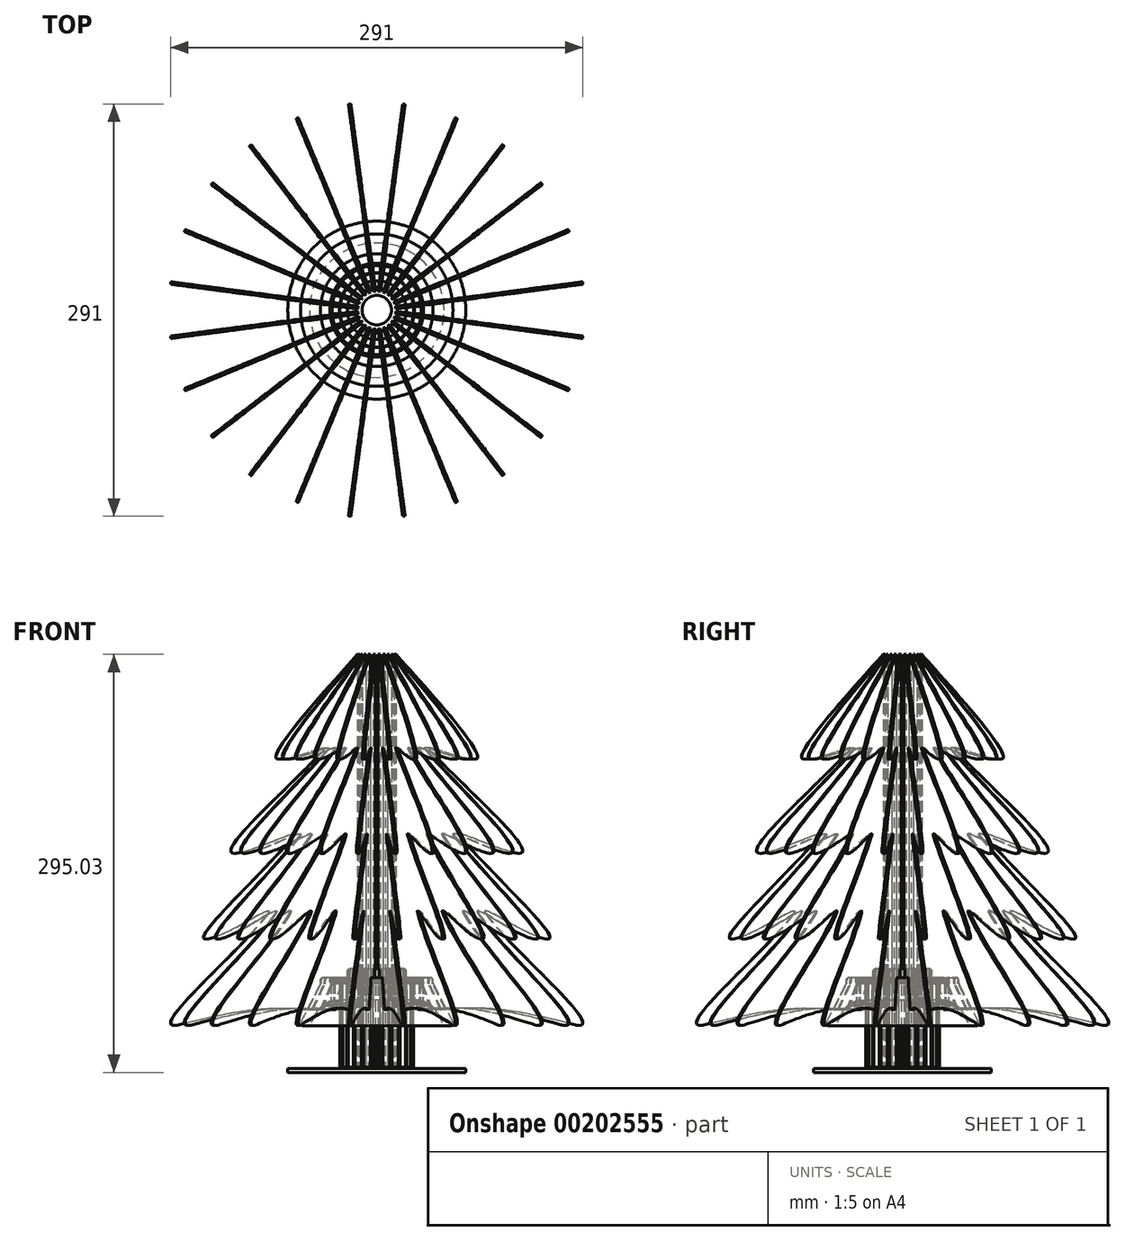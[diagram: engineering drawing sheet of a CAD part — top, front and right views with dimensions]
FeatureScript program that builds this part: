
annotation { "Feature Type Name" : "Feature", "Feature Type Description" : "" }
export const myFeature = defineFeature(function(context is Context, id is Id, definition is map)
    precondition{}
    {
        {
            var Q0;
            Q0=qCreatedBy(makeId("Top.planeOp"),FACE);
            var sketch = newSketch(context, id + "F0", { "sketchPlane" : qUnion([Q0])});
            skCircle(sketch, "E0", {"center": v(0, 0) * mm, "radius": 32.75 * mm});
            skCircle(sketch, "E1", {"center": v(0, 0) * mm, "radius": 26.1 * mm});
            skSolve(sketch);
        }
        {
            var Q0;
            Q0=qSketchRegion(id+"F0",true);
            extrude(context, id + "F1", {"entities" : qUnion([Q0]), "depth" : 1.65 * mm});
        }
        {
            var Q0;
            Q0=makeQuery(id+"F1.opExtrude","CAP_FACE",FACE,{"disambiguationData":[OSD([sQuery(id+"F0.wireOp",EDGE,"E0"),sQuery(id+"F0.wireOp",EDGE,"E1")])],"isStart":false});
            var sketch = newSketch(context, id + "F2", { "sketchPlane" : qUnion([Q0])});
            skLineSegment(sketch, "E2.bottom", {"start": v(2.5, -26.5) * mm, "end": v(-2.5, -26.5) * mm});
            skLineSegment(sketch, "E2.top", {"start": v(2.5, -31.5) * mm, "end": v(-2.5, -31.5) * mm});
            skLineSegment(sketch, "E2.left", {"start": v(2.5, -26.5) * mm, "end": v(2.5, -31.5) * mm});
            skLineSegment(sketch, "E2.right", {"start": v(-2.5, -26.5) * mm, "end": v(-2.5, -31.5) * mm});
            skPoint(sketch, "E2.middle", {"position": v(0, -29) * mm});
            skSolve(sketch);
        }
        {
            var Q0;
            Q0=makeQuery(id+"F2.imprint","IMPRINT",FACE,{"disambiguationData":[TD([[makeQuery(id+"F2.imprint","IMPRINT",EDGE,{"derivedFrom":sQuery(id+"F2.wireOp",EDGE,"E2.bottom")}),1.0]])]});
            extrude(context, id + "F3", {"entities" : qUnion([Q0]), "depth" : 1.62 * mm});
        }
        {
            var Q0;
            Q0=makeQuery(id+"F3.opExtrude","SWEPT_BODY",BODY,{"disambiguationData":[OSD([sQuery(id+"F2.wireOp",EDGE,"E2.bottom"),sQuery(id+"F2.wireOp",EDGE,"E2.top"),sQuery(id+"F2.wireOp",EDGE,"E2.left"),sQuery(id+"F2.wireOp",EDGE,"E2.right")])]});
            var Q1;
            Q1=makeQuery(id+"F1.opExtrude","CAP_EDGE",EDGE,{"disambiguationData":[OSD([sQuery(id+"F0.wireOp",EDGE,"E0")])],"isStart":false});
            circularPattern(context, id + "F4", {"entities" : qUnion([Q0]), "axis" : qUnion([Q1]), "angle" : 360 * degree, "instanceCount" : 24, "equalSpace" : true});
        }
        {
            var Q0;
            Q0=qCreatedBy(makeId("Front.planeOp"),FACE);
            var sketch = newSketch(context, id + "F5", { "sketchPlane" : qUnion([Q0])});
            skFitSpline(sketch, "E3", {"points": [v(-35, 220) * mm, v(-100, 30) * mm, v(-35, 0) * mm, v(-35, -60) * mm], "startDerivative": vector(15.54, -139.11) * mm, "endDerivative": vector(560.9, -352.96) * mm});
            skLineSegment(sketch, "E4", {"start": v(-9.97, -59.99) * mm, "end": v(-9.97, -0.01) * mm, "construction": true});
            skLineSegment(sketch, "E5", {"start": v(-9.97, -0.01) * mm, "end": v(-33, -0.01) * mm});
            skLineSegment(sketch, "E6", {"start": v(-33, -0.01) * mm, "end": v(-33, 3.46) * mm});
            skLineSegment(sketch, "E7", {"start": v(-33, 3.46) * mm, "end": v(0, 3.46) * mm});
            skLineSegment(sketch, "E8", {"start": v(0, 3.46) * mm, "end": v(0, 369.62) * mm, "construction": true});
            skLineSegment(sketch, "E9", {"start": v(-5, 3.46) * mm, "end": v(-5, 220) * mm, "construction": true});
            skFitSpline(sketch, "E10", {"points": [v(-5, -60) * mm, v(-5, 0) * mm, v(-70, 30) * mm, v(-5, 220) * mm], "startDerivative": vector(-560.9, 352.96) * mm, "endDerivative": vector(-15.54, 139.11) * mm});
            skLineSegment(sketch, "E11", {"start": v(-35, -60) * mm, "end": v(-5, -60) * mm});
            skLineSegment(sketch, "E12", {"start": v(-82.67, -30) * mm, "end": v(-52.67, -30) * mm, "construction": true});
            skLineSegment(sketch, "E13", {"start": v(-35, 0) * mm, "end": v(-5, 0) * mm, "construction": true});
            skLineSegment(sketch, "E14", {"start": v(-35, 220) * mm, "end": v(-5, 220) * mm});
            skLineSegment(sketch, "E15", {"start": v(-32.58, 198.37) * mm, "end": v(-2.58, 198.37) * mm, "construction": true});
            skLineSegment(sketch, "E16", {"start": v(-100, 30) * mm, "end": v(-70, 30) * mm, "construction": true});
            skPoint(sketch, "E17", {"position": v(-9.97, -30) * mm});
            skSolve(sketch);
        }
        {
            var Q0;
            Q0=qCreatedBy(makeId("Front.planeOp"),FACE);
            var sketch = newSketch(context, id + "F6", { "sketchPlane" : qUnion([Q0])});
            skFitSpline(sketch, "E18", {"points": [v(13.6, 232.09) * mm, v(70.8, 158.19) * mm], "startDerivative": vector(38.38, -42.53) * mm, "endDerivative": vector(-27.12, -7.4) * mm});
            skFitSpline(sketch, "E19", {"points": [v(70.8, 158.19) * mm, v(37.61, 164.6) * mm], "startDerivative": vector(-30.94, -4.18) * mm, "endDerivative": vector(18.16, -18.68) * mm});
            skFitSpline(sketch, "E20", {"points": [v(37.61, 164.6) * mm, v(100.47, 91.7) * mm], "startDerivative": vector(70.23, -76.21) * mm, "endDerivative": vector(-53.14, 3.33) * mm});
            skFitSpline(sketch, "E21", {"points": [v(100.47, 91.7) * mm, v(59.62, 103.15) * mm], "startDerivative": vector(-49.24, 6.98) * mm, "endDerivative": vector(24.28, -25.46) * mm});
            skFitSpline(sketch, "E22", {"points": [v(59.62, 103.15) * mm, v(121.17, 31.14) * mm], "startDerivative": vector(76.76, -89.28) * mm, "endDerivative": vector(-37.88, 2.63) * mm});
            skFitSpline(sketch, "E23", {"points": [v(121.17, 31.14) * mm, v(78.02, 48.42) * mm], "startDerivative": vector(-45.72, 5.53) * mm, "endDerivative": vector(24.28, -33.22) * mm});
            skFitSpline(sketch, "E24", {"points": [v(78.02, 48.42) * mm, v(142.48, -29.72) * mm], "startDerivative": vector(61.84, -82.84) * mm, "endDerivative": vector(-63.39, 7.82) * mm});
            skFitSpline(sketch, "E25", {"points": [v(142.48, -29.72) * mm, v(32.75, -14.43) * mm], "startDerivative": vector(-262.82, 70.32) * mm, "endDerivative": vector(-71.27, 35.61) * mm});
            skLineSegment(sketch, "E26", {"start": v(13.6, 232.09) * mm, "end": v(13.6, -59.36) * mm});
            skLineSegment(sketch, "E27", {"start": v(13.6, -59.36) * mm, "end": v(26.1, -59.36) * mm});
            skLineSegment(sketch, "E28", {"start": v(26.1, -59.36) * mm, "end": v(26.1, 1.65) * mm});
            skLineSegment(sketch, "E29", {"start": v(26.1, 1.65) * mm, "end": v(32.75, 1.65) * mm});
            skLineSegment(sketch, "E30", {"start": v(32.75, 1.65) * mm, "end": v(32.75, -14.43) * mm});
            skSolve(sketch);
        }
        {
            var Q0;
            Q0=makeQuery(id+"F6.imprint","IMPRINT",FACE,{"disambiguationData":[TD([[makeQuery(id+"F6.imprint","IMPRINT",EDGE,{"derivedFrom":sQuery(id+"F6.wireOp",EDGE,"E18")}),-1.0]])]});
            extrude(context, id + "F7", {"entities" : qUnion([Q0]), "endBound" : BoundingType.SYMMETRIC, "depth" : 1.7 * mm});
        }
        {
            var Q0;
            Q0=makeQuery(id+"Fo9Mr46O54dBFXy_3.opExtrude","SWEPT_BODY",BODY,{"disambiguationData":[OSD([sQuery(id+"F5.wireOp",EDGE,"E3"),sQuery(id+"F5.wireOp",EDGE,"E5"),sQuery(id+"F5.wireOp",EDGE,"E6"),sQuery(id+"F5.wireOp",EDGE,"E7"),sQuery(id+"F5.wireOp",EDGE,"E10"),sQuery(id+"F5.wireOp",EDGE,"E11"),sQuery(id+"F5.wireOp",EDGE,"E14")])]});
            var Q1;
            Q1=makeQuery(id+"F7.opExtrude","SWEPT_BODY",BODY,{"disambiguationData":[OSD([sQuery(id+"F6.wireOp",EDGE,"E18"),sQuery(id+"F6.wireOp",EDGE,"E19"),sQuery(id+"F6.wireOp",EDGE,"E20"),sQuery(id+"F6.wireOp",EDGE,"E21"),sQuery(id+"F6.wireOp",EDGE,"E22"),sQuery(id+"F6.wireOp",EDGE,"E23"),sQuery(id+"F6.wireOp",EDGE,"E24"),sQuery(id+"F6.wireOp",EDGE,"E25"),sQuery(id+"F6.wireOp",EDGE,"E26"),sQuery(id+"F6.wireOp",EDGE,"E27"),sQuery(id+"F6.wireOp",EDGE,"E28"),sQuery(id+"F6.wireOp",EDGE,"E29"),sQuery(id+"F6.wireOp",EDGE,"E30")])]});
            var Q2;
            Q2=sQuery(id+"F5.wireOp",EDGE,"E8");
            transform(context, id + "F8", {"entities" : qUnion([Q0, Q1]), "transformType" : TransformType.ROTATION, "transformAxis" : qUnion([Q2]), "angle" : 7.5 * degree, "makeCopy" : false});
        }
        {
            var Q0;
            Q0=makeQuery(id+"F7.opExtrude","SWEPT_BODY",BODY,{"disambiguationData":[OSD([sQuery(id+"F6.wireOp",EDGE,"E18"),sQuery(id+"F6.wireOp",EDGE,"E19"),sQuery(id+"F6.wireOp",EDGE,"E20"),sQuery(id+"F6.wireOp",EDGE,"E21"),sQuery(id+"F6.wireOp",EDGE,"E22"),sQuery(id+"F6.wireOp",EDGE,"E23"),sQuery(id+"F6.wireOp",EDGE,"E24"),sQuery(id+"F6.wireOp",EDGE,"E25"),sQuery(id+"F6.wireOp",EDGE,"E26"),sQuery(id+"F6.wireOp",EDGE,"E27"),sQuery(id+"F6.wireOp",EDGE,"E28"),sQuery(id+"F6.wireOp",EDGE,"E29"),sQuery(id+"F6.wireOp",EDGE,"E30")])]});
            var Q1;
            Q1=sQuery(id+"F5.wireOp",EDGE,"E8");
            circularPattern(context, id + "F9", {"entities" : qUnion([Q0]), "axis" : qUnion([Q1]), "angle" : 360 * degree, "instanceCount" : 24, "equalSpace" : true});
        }
        {
            var Q0;
            Q0=qCreatedBy(makeId("Front.planeOp"),FACE);
            var sketch = newSketch(context, id + "F10", { "sketchPlane" : qUnion([Q0])});
            skLineSegment(sketch, "E31", {"start": v(0, -60.33) * mm, "end": v(-70.34, -60.33) * mm});
            skLineSegment(sketch, "E32", {"start": v(-70.34, -60.33) * mm, "end": v(-39.68, 0) * mm});
            skLineSegment(sketch, "E33", {"start": v(-39.68, 0) * mm, "end": v(-20.78, 0) * mm});
            skLineSegment(sketch, "E34", {"start": v(-20.78, 0) * mm, "end": v(-20.78, 10.18) * mm});
            skLineSegment(sketch, "E35", {"start": v(-20.78, 10.18) * mm, "end": v(0, 10.18) * mm});
            skLineSegment(sketch, "E36", {"start": v(0, 10.18) * mm, "end": v(0, -60.33) * mm});
            skLineSegment(sketch, "E37", {"start": v(-62.79, -60.33) * mm, "end": v(-62.79, -62.94) * mm});
            skLineSegment(sketch, "E38", {"start": v(-62.79, -62.94) * mm, "end": v(0, -62.94) * mm});
            skLineSegment(sketch, "E39", {"start": v(0, -62.94) * mm, "end": v(0, -60.33) * mm});
            skLineSegment(sketch, "E40", {"start": v(-33.07, 0) * mm, "end": v(-33.07, 4.07) * mm});
            skLineSegment(sketch, "E41", {"start": v(-33.07, 4.07) * mm, "end": v(-39.68, 4.07) * mm});
            skLineSegment(sketch, "E42", {"start": v(-39.68, 4.07) * mm, "end": v(-39.68, 0) * mm});
            skLineSegment(sketch, "E43", {"start": v(-20.78, 0.85) * mm, "end": v(-39.68, 0.85) * mm});
            skLineSegment(sketch, "E44", {"start": v(-10.4, 10.18) * mm, "end": v(-10.4, -11.98) * mm});
            skLineSegment(sketch, "E45", {"start": v(-10.4, -11.98) * mm, "end": v(-38.22, -11.98) * mm});
            skLineSegment(sketch, "E46", {"start": v(-38.22, -11.98) * mm, "end": v(-62.79, -60.33) * mm});
            skLineSegment(sketch, "E47", {"start": v(-55.01, -30.16) * mm, "end": v(0, -30.16) * mm});
            skSolve(sketch);
        }
        {
            var Q0;
            {var subQ2=sQuery(id+"F10.wireOp",EDGE,"E37");Q0=makeQuery(id+"F10.imprint","IMPRINT",FACE,{"disambiguationData":[TD([[makeQuery(id+"F10.imprint","IMPRINT",EDGE,{"derivedFrom":subQ2}),1.0]])]});}
            var Q1;
            {var subQ2=sQuery(id+"F10.wireOp",EDGE,"E40");Q1=makeQuery(id+"F10.imprint","IMPRINT",FACE,{"disambiguationData":[TD([[makeQuery(id+"F10.imprint","IMPRINT",EDGE,{"derivedFrom":subQ2}),1.0]])]});}
            var Q2;
            {var subQ0=sQuery(id+"F10.wireOp",EDGE,"E34");var subQ1=sQuery(id+"F10.wireOp",EDGE,"E33");var subQ2=makeQuery(id+"F10.imprint","INTERSECT",VERTEX,{"derivedFrom":[subQ1,subQ0]});Q2=makeQuery(id+"F10.imprint","IMPRINT",FACE,{"disambiguationData":[TD([[makeQuery(id+"F10.imprint","IMPRINT",EDGE,{"disambiguationData":[TD([[subQ2,1.0]])],"derivedFrom":subQ1}),1.0]])]});}
            var Q3;
            {var subQ13=sQuery(id+"F10.wireOp",EDGE,"E44");Q3=makeQuery(id+"F10.imprint","IMPRINT",FACE,{"disambiguationData":[TD([[makeQuery(id+"F10.imprint","IMPRINT",EDGE,{"derivedFrom":subQ13}),-1.0]])]});}
            var Q4;
            Q4=sQuery(id+"F10.wireOp",EDGE,"E36");
            revolve(context, id + "F11", {"entities" : qUnion([Q0, Q1, Q2, Q3]), "axis" : qUnion([Q4]), "revolveType" : RevolveType.FULL});
        }
        {
            var Q0;
            Q0=makeQuery(id+"F11.opRevolve","SWEPT_EDGE",EDGE,{"disambiguationData":[OSD([sQuery(id+"F10.wireOp",EDGE,"E32"),sQuery(id+"F10.wireOp",EDGE,"E33"),sQuery(id+"F10.wireOp",EDGE,"E42")])]});
            var Q1;
            Q1=makeQuery(id+"F11.opRevolve","SWEPT_EDGE",EDGE,{"disambiguationData":[OSD([sQuery(id+"F10.wireOp",EDGE,"E41"),sQuery(id+"F10.wireOp",EDGE,"E42")])]});
            var Q2;
            Q2=makeQuery(id+"F11.opRevolve","SWEPT_EDGE",EDGE,{"disambiguationData":[OSD([sQuery(id+"F10.wireOp",EDGE,"E34"),sQuery(id+"F10.wireOp",EDGE,"E35")])]});
            var Q3;
            Q3=makeQuery(id+"F11.opRevolve","SWEPT_EDGE",EDGE,{"disambiguationData":[OSD([sQuery(id+"F10.wireOp",EDGE,"E35"),sQuery(id+"F10.wireOp",EDGE,"E44")])]});
            var Q4;
            Q4=makeQuery(id+"F11.opRevolve","SWEPT_EDGE",EDGE,{"disambiguationData":[OSD([sQuery(id+"F10.wireOp",EDGE,"E31"),sQuery(id+"F10.wireOp",EDGE,"E32")])]});
            fillet(context, id + "F12", {"entities" : qUnion([Q0, Q1, Q2, Q3, Q4]), "radius" : 2 * mm, "tangentPropagation" : true, "allowEdgeOverflow" : false});
        }
        {
            var Q0;
            Q0=makeQuery(id+"F11.opRevolve","SWEPT_EDGE",EDGE,{"disambiguationData":[OSD([sQuery(id+"F10.wireOp",EDGE,"E40"),sQuery(id+"F10.wireOp",EDGE,"E41")])]});
            fillet(context, id + "F13", {"entities" : qUnion([Q0]), "radius" : .5 * mm, "tangentPropagation" : true, "allowEdgeOverflow" : false});
        }
        {
            var Q0;
            Q0=makeQuery(id+"F11.opRevolve","SWEPT_EDGE",EDGE,{"disambiguationData":[OSD([sQuery(id+"F10.wireOp",EDGE,"E45"),sQuery(id+"F10.wireOp",EDGE,"E46")])]});
            fillet(context, id + "F14", {"entities" : qUnion([Q0]), "radius" : 16.74 * mm, "tangentPropagation" : true, "allowEdgeOverflow" : false});
        }
        {
            var Q0;
            Q0=makeQuery(id+"F1.opExtrude","SWEPT_BODY",BODY,{"disambiguationData":[OSD([sQuery(id+"F0.wireOp",EDGE,"E0"),sQuery(id+"F0.wireOp",EDGE,"E1")])]});
            var Q1;
            Q1=makeQuery(id+"F9.opPattern","COPY",BODY,{"derivedFrom":makeQuery(id+"F7.opExtrude","SWEPT_BODY",BODY,{"disambiguationData":[OSD([sQuery(id+"F6.wireOp",EDGE,"E18"),sQuery(id+"F6.wireOp",EDGE,"E19"),sQuery(id+"F6.wireOp",EDGE,"E20"),sQuery(id+"F6.wireOp",EDGE,"E21"),sQuery(id+"F6.wireOp",EDGE,"E22"),sQuery(id+"F6.wireOp",EDGE,"E23"),sQuery(id+"F6.wireOp",EDGE,"E24"),sQuery(id+"F6.wireOp",EDGE,"E25"),sQuery(id+"F6.wireOp",EDGE,"E26"),sQuery(id+"F6.wireOp",EDGE,"E27"),sQuery(id+"F6.wireOp",EDGE,"E28"),sQuery(id+"F6.wireOp",EDGE,"E29"),sQuery(id+"F6.wireOp",EDGE,"E30")])]}),"instanceName":"3"});
            var Q2;
            Q2=makeQuery(id+"F9.opPattern","COPY",BODY,{"derivedFrom":makeQuery(id+"F7.opExtrude","SWEPT_BODY",BODY,{"disambiguationData":[OSD([sQuery(id+"F6.wireOp",EDGE,"E18"),sQuery(id+"F6.wireOp",EDGE,"E19"),sQuery(id+"F6.wireOp",EDGE,"E20"),sQuery(id+"F6.wireOp",EDGE,"E21"),sQuery(id+"F6.wireOp",EDGE,"E22"),sQuery(id+"F6.wireOp",EDGE,"E23"),sQuery(id+"F6.wireOp",EDGE,"E24"),sQuery(id+"F6.wireOp",EDGE,"E25"),sQuery(id+"F6.wireOp",EDGE,"E26"),sQuery(id+"F6.wireOp",EDGE,"E27"),sQuery(id+"F6.wireOp",EDGE,"E28"),sQuery(id+"F6.wireOp",EDGE,"E29"),sQuery(id+"F6.wireOp",EDGE,"E30")])]}),"instanceName":"4"});
            var Q3;
            Q3=makeQuery(id+"F9.opPattern","COPY",BODY,{"derivedFrom":makeQuery(id+"F7.opExtrude","SWEPT_BODY",BODY,{"disambiguationData":[OSD([sQuery(id+"F6.wireOp",EDGE,"E18"),sQuery(id+"F6.wireOp",EDGE,"E19"),sQuery(id+"F6.wireOp",EDGE,"E20"),sQuery(id+"F6.wireOp",EDGE,"E21"),sQuery(id+"F6.wireOp",EDGE,"E22"),sQuery(id+"F6.wireOp",EDGE,"E23"),sQuery(id+"F6.wireOp",EDGE,"E24"),sQuery(id+"F6.wireOp",EDGE,"E25"),sQuery(id+"F6.wireOp",EDGE,"E26"),sQuery(id+"F6.wireOp",EDGE,"E27"),sQuery(id+"F6.wireOp",EDGE,"E28"),sQuery(id+"F6.wireOp",EDGE,"E29"),sQuery(id+"F6.wireOp",EDGE,"E30")])]}),"instanceName":"5"});
            var Q4;
            Q4=makeQuery(id+"F9.opPattern","COPY",BODY,{"derivedFrom":makeQuery(id+"F7.opExtrude","SWEPT_BODY",BODY,{"disambiguationData":[OSD([sQuery(id+"F6.wireOp",EDGE,"E18"),sQuery(id+"F6.wireOp",EDGE,"E19"),sQuery(id+"F6.wireOp",EDGE,"E20"),sQuery(id+"F6.wireOp",EDGE,"E21"),sQuery(id+"F6.wireOp",EDGE,"E22"),sQuery(id+"F6.wireOp",EDGE,"E23"),sQuery(id+"F6.wireOp",EDGE,"E24"),sQuery(id+"F6.wireOp",EDGE,"E25"),sQuery(id+"F6.wireOp",EDGE,"E26"),sQuery(id+"F6.wireOp",EDGE,"E27"),sQuery(id+"F6.wireOp",EDGE,"E28"),sQuery(id+"F6.wireOp",EDGE,"E29"),sQuery(id+"F6.wireOp",EDGE,"E30")])]}),"instanceName":"6"});
            var Q5;
            Q5=makeQuery(id+"F9.opPattern","COPY",BODY,{"derivedFrom":makeQuery(id+"F7.opExtrude","SWEPT_BODY",BODY,{"disambiguationData":[OSD([sQuery(id+"F6.wireOp",EDGE,"E18"),sQuery(id+"F6.wireOp",EDGE,"E19"),sQuery(id+"F6.wireOp",EDGE,"E20"),sQuery(id+"F6.wireOp",EDGE,"E21"),sQuery(id+"F6.wireOp",EDGE,"E22"),sQuery(id+"F6.wireOp",EDGE,"E23"),sQuery(id+"F6.wireOp",EDGE,"E24"),sQuery(id+"F6.wireOp",EDGE,"E25"),sQuery(id+"F6.wireOp",EDGE,"E26"),sQuery(id+"F6.wireOp",EDGE,"E27"),sQuery(id+"F6.wireOp",EDGE,"E28"),sQuery(id+"F6.wireOp",EDGE,"E29"),sQuery(id+"F6.wireOp",EDGE,"E30")])]}),"instanceName":"7"});
            var Q6;
            Q6=makeQuery(id+"F9.opPattern","COPY",BODY,{"derivedFrom":makeQuery(id+"F7.opExtrude","SWEPT_BODY",BODY,{"disambiguationData":[OSD([sQuery(id+"F6.wireOp",EDGE,"E18"),sQuery(id+"F6.wireOp",EDGE,"E19"),sQuery(id+"F6.wireOp",EDGE,"E20"),sQuery(id+"F6.wireOp",EDGE,"E21"),sQuery(id+"F6.wireOp",EDGE,"E22"),sQuery(id+"F6.wireOp",EDGE,"E23"),sQuery(id+"F6.wireOp",EDGE,"E24"),sQuery(id+"F6.wireOp",EDGE,"E25"),sQuery(id+"F6.wireOp",EDGE,"E26"),sQuery(id+"F6.wireOp",EDGE,"E27"),sQuery(id+"F6.wireOp",EDGE,"E28"),sQuery(id+"F6.wireOp",EDGE,"E29"),sQuery(id+"F6.wireOp",EDGE,"E30")])]}),"instanceName":"8"});
            var Q7;
            Q7=makeQuery(id+"F9.opPattern","COPY",BODY,{"derivedFrom":makeQuery(id+"F7.opExtrude","SWEPT_BODY",BODY,{"disambiguationData":[OSD([sQuery(id+"F6.wireOp",EDGE,"E18"),sQuery(id+"F6.wireOp",EDGE,"E19"),sQuery(id+"F6.wireOp",EDGE,"E20"),sQuery(id+"F6.wireOp",EDGE,"E21"),sQuery(id+"F6.wireOp",EDGE,"E22"),sQuery(id+"F6.wireOp",EDGE,"E23"),sQuery(id+"F6.wireOp",EDGE,"E24"),sQuery(id+"F6.wireOp",EDGE,"E25"),sQuery(id+"F6.wireOp",EDGE,"E26"),sQuery(id+"F6.wireOp",EDGE,"E27"),sQuery(id+"F6.wireOp",EDGE,"E28"),sQuery(id+"F6.wireOp",EDGE,"E29"),sQuery(id+"F6.wireOp",EDGE,"E30")])]}),"instanceName":"9"});
            var Q8;
            Q8=makeQuery(id+"F9.opPattern","COPY",BODY,{"derivedFrom":makeQuery(id+"F7.opExtrude","SWEPT_BODY",BODY,{"disambiguationData":[OSD([sQuery(id+"F6.wireOp",EDGE,"E18"),sQuery(id+"F6.wireOp",EDGE,"E19"),sQuery(id+"F6.wireOp",EDGE,"E20"),sQuery(id+"F6.wireOp",EDGE,"E21"),sQuery(id+"F6.wireOp",EDGE,"E22"),sQuery(id+"F6.wireOp",EDGE,"E23"),sQuery(id+"F6.wireOp",EDGE,"E24"),sQuery(id+"F6.wireOp",EDGE,"E25"),sQuery(id+"F6.wireOp",EDGE,"E26"),sQuery(id+"F6.wireOp",EDGE,"E27"),sQuery(id+"F6.wireOp",EDGE,"E28"),sQuery(id+"F6.wireOp",EDGE,"E29"),sQuery(id+"F6.wireOp",EDGE,"E30")])]}),"instanceName":"10"});
            var Q9;
            Q9=makeQuery(id+"F9.opPattern","COPY",BODY,{"derivedFrom":makeQuery(id+"F7.opExtrude","SWEPT_BODY",BODY,{"disambiguationData":[OSD([sQuery(id+"F6.wireOp",EDGE,"E18"),sQuery(id+"F6.wireOp",EDGE,"E19"),sQuery(id+"F6.wireOp",EDGE,"E20"),sQuery(id+"F6.wireOp",EDGE,"E21"),sQuery(id+"F6.wireOp",EDGE,"E22"),sQuery(id+"F6.wireOp",EDGE,"E23"),sQuery(id+"F6.wireOp",EDGE,"E24"),sQuery(id+"F6.wireOp",EDGE,"E25"),sQuery(id+"F6.wireOp",EDGE,"E26"),sQuery(id+"F6.wireOp",EDGE,"E27"),sQuery(id+"F6.wireOp",EDGE,"E28"),sQuery(id+"F6.wireOp",EDGE,"E29"),sQuery(id+"F6.wireOp",EDGE,"E30")])]}),"instanceName":"11"});
            var Q10;
            Q10=makeQuery(id+"F9.opPattern","COPY",BODY,{"derivedFrom":makeQuery(id+"F7.opExtrude","SWEPT_BODY",BODY,{"disambiguationData":[OSD([sQuery(id+"F6.wireOp",EDGE,"E18"),sQuery(id+"F6.wireOp",EDGE,"E19"),sQuery(id+"F6.wireOp",EDGE,"E20"),sQuery(id+"F6.wireOp",EDGE,"E21"),sQuery(id+"F6.wireOp",EDGE,"E22"),sQuery(id+"F6.wireOp",EDGE,"E23"),sQuery(id+"F6.wireOp",EDGE,"E24"),sQuery(id+"F6.wireOp",EDGE,"E25"),sQuery(id+"F6.wireOp",EDGE,"E26"),sQuery(id+"F6.wireOp",EDGE,"E27"),sQuery(id+"F6.wireOp",EDGE,"E28"),sQuery(id+"F6.wireOp",EDGE,"E29"),sQuery(id+"F6.wireOp",EDGE,"E30")])]}),"instanceName":"12"});
            var Q11;
            Q11=makeQuery(id+"F9.opPattern","COPY",BODY,{"derivedFrom":makeQuery(id+"F7.opExtrude","SWEPT_BODY",BODY,{"disambiguationData":[OSD([sQuery(id+"F6.wireOp",EDGE,"E18"),sQuery(id+"F6.wireOp",EDGE,"E19"),sQuery(id+"F6.wireOp",EDGE,"E20"),sQuery(id+"F6.wireOp",EDGE,"E21"),sQuery(id+"F6.wireOp",EDGE,"E22"),sQuery(id+"F6.wireOp",EDGE,"E23"),sQuery(id+"F6.wireOp",EDGE,"E24"),sQuery(id+"F6.wireOp",EDGE,"E25"),sQuery(id+"F6.wireOp",EDGE,"E26"),sQuery(id+"F6.wireOp",EDGE,"E27"),sQuery(id+"F6.wireOp",EDGE,"E28"),sQuery(id+"F6.wireOp",EDGE,"E29"),sQuery(id+"F6.wireOp",EDGE,"E30")])]}),"instanceName":"13"});
            var Q12;
            Q12=makeQuery(id+"F9.opPattern","COPY",BODY,{"derivedFrom":makeQuery(id+"F7.opExtrude","SWEPT_BODY",BODY,{"disambiguationData":[OSD([sQuery(id+"F6.wireOp",EDGE,"E18"),sQuery(id+"F6.wireOp",EDGE,"E19"),sQuery(id+"F6.wireOp",EDGE,"E20"),sQuery(id+"F6.wireOp",EDGE,"E21"),sQuery(id+"F6.wireOp",EDGE,"E22"),sQuery(id+"F6.wireOp",EDGE,"E23"),sQuery(id+"F6.wireOp",EDGE,"E24"),sQuery(id+"F6.wireOp",EDGE,"E25"),sQuery(id+"F6.wireOp",EDGE,"E26"),sQuery(id+"F6.wireOp",EDGE,"E27"),sQuery(id+"F6.wireOp",EDGE,"E28"),sQuery(id+"F6.wireOp",EDGE,"E29"),sQuery(id+"F6.wireOp",EDGE,"E30")])]}),"instanceName":"14"});
            var Q13;
            Q13=makeQuery(id+"F9.opPattern","COPY",BODY,{"derivedFrom":makeQuery(id+"F7.opExtrude","SWEPT_BODY",BODY,{"disambiguationData":[OSD([sQuery(id+"F6.wireOp",EDGE,"E18"),sQuery(id+"F6.wireOp",EDGE,"E19"),sQuery(id+"F6.wireOp",EDGE,"E20"),sQuery(id+"F6.wireOp",EDGE,"E21"),sQuery(id+"F6.wireOp",EDGE,"E22"),sQuery(id+"F6.wireOp",EDGE,"E23"),sQuery(id+"F6.wireOp",EDGE,"E24"),sQuery(id+"F6.wireOp",EDGE,"E25"),sQuery(id+"F6.wireOp",EDGE,"E26"),sQuery(id+"F6.wireOp",EDGE,"E27"),sQuery(id+"F6.wireOp",EDGE,"E28"),sQuery(id+"F6.wireOp",EDGE,"E29"),sQuery(id+"F6.wireOp",EDGE,"E30")])]}),"instanceName":"15"});
            var Q14;
            Q14=makeQuery(id+"F9.opPattern","COPY",BODY,{"derivedFrom":makeQuery(id+"F7.opExtrude","SWEPT_BODY",BODY,{"disambiguationData":[OSD([sQuery(id+"F6.wireOp",EDGE,"E18"),sQuery(id+"F6.wireOp",EDGE,"E19"),sQuery(id+"F6.wireOp",EDGE,"E20"),sQuery(id+"F6.wireOp",EDGE,"E21"),sQuery(id+"F6.wireOp",EDGE,"E22"),sQuery(id+"F6.wireOp",EDGE,"E23"),sQuery(id+"F6.wireOp",EDGE,"E24"),sQuery(id+"F6.wireOp",EDGE,"E25"),sQuery(id+"F6.wireOp",EDGE,"E26"),sQuery(id+"F6.wireOp",EDGE,"E27"),sQuery(id+"F6.wireOp",EDGE,"E28"),sQuery(id+"F6.wireOp",EDGE,"E29"),sQuery(id+"F6.wireOp",EDGE,"E30")])]}),"instanceName":"16"});
            var Q15;
            Q15=makeQuery(id+"F9.opPattern","COPY",BODY,{"derivedFrom":makeQuery(id+"F7.opExtrude","SWEPT_BODY",BODY,{"disambiguationData":[OSD([sQuery(id+"F6.wireOp",EDGE,"E18"),sQuery(id+"F6.wireOp",EDGE,"E19"),sQuery(id+"F6.wireOp",EDGE,"E20"),sQuery(id+"F6.wireOp",EDGE,"E21"),sQuery(id+"F6.wireOp",EDGE,"E22"),sQuery(id+"F6.wireOp",EDGE,"E23"),sQuery(id+"F6.wireOp",EDGE,"E24"),sQuery(id+"F6.wireOp",EDGE,"E25"),sQuery(id+"F6.wireOp",EDGE,"E26"),sQuery(id+"F6.wireOp",EDGE,"E27"),sQuery(id+"F6.wireOp",EDGE,"E28"),sQuery(id+"F6.wireOp",EDGE,"E29"),sQuery(id+"F6.wireOp",EDGE,"E30")])]}),"instanceName":"17"});
            var Q16;
            Q16=makeQuery(id+"F9.opPattern","COPY",BODY,{"derivedFrom":makeQuery(id+"F7.opExtrude","SWEPT_BODY",BODY,{"disambiguationData":[OSD([sQuery(id+"F6.wireOp",EDGE,"E18"),sQuery(id+"F6.wireOp",EDGE,"E19"),sQuery(id+"F6.wireOp",EDGE,"E20"),sQuery(id+"F6.wireOp",EDGE,"E21"),sQuery(id+"F6.wireOp",EDGE,"E22"),sQuery(id+"F6.wireOp",EDGE,"E23"),sQuery(id+"F6.wireOp",EDGE,"E24"),sQuery(id+"F6.wireOp",EDGE,"E25"),sQuery(id+"F6.wireOp",EDGE,"E26"),sQuery(id+"F6.wireOp",EDGE,"E27"),sQuery(id+"F6.wireOp",EDGE,"E28"),sQuery(id+"F6.wireOp",EDGE,"E29"),sQuery(id+"F6.wireOp",EDGE,"E30")])]}),"instanceName":"21"});
            var Q17;
            Q17=makeQuery(id+"F7.opExtrude","SWEPT_BODY",BODY,{"disambiguationData":[OSD([sQuery(id+"F6.wireOp",EDGE,"E18"),sQuery(id+"F6.wireOp",EDGE,"E19"),sQuery(id+"F6.wireOp",EDGE,"E20"),sQuery(id+"F6.wireOp",EDGE,"E21"),sQuery(id+"F6.wireOp",EDGE,"E22"),sQuery(id+"F6.wireOp",EDGE,"E23"),sQuery(id+"F6.wireOp",EDGE,"E24"),sQuery(id+"F6.wireOp",EDGE,"E25"),sQuery(id+"F6.wireOp",EDGE,"E26"),sQuery(id+"F6.wireOp",EDGE,"E27"),sQuery(id+"F6.wireOp",EDGE,"E28"),sQuery(id+"F6.wireOp",EDGE,"E29"),sQuery(id+"F6.wireOp",EDGE,"E30")])]});
            var Q18;
            Q18=makeQuery(id+"F9.opPattern","COPY",BODY,{"derivedFrom":makeQuery(id+"F7.opExtrude","SWEPT_BODY",BODY,{"disambiguationData":[OSD([sQuery(id+"F6.wireOp",EDGE,"E18"),sQuery(id+"F6.wireOp",EDGE,"E19"),sQuery(id+"F6.wireOp",EDGE,"E20"),sQuery(id+"F6.wireOp",EDGE,"E21"),sQuery(id+"F6.wireOp",EDGE,"E22"),sQuery(id+"F6.wireOp",EDGE,"E23"),sQuery(id+"F6.wireOp",EDGE,"E24"),sQuery(id+"F6.wireOp",EDGE,"E25"),sQuery(id+"F6.wireOp",EDGE,"E26"),sQuery(id+"F6.wireOp",EDGE,"E27"),sQuery(id+"F6.wireOp",EDGE,"E28"),sQuery(id+"F6.wireOp",EDGE,"E29"),sQuery(id+"F6.wireOp",EDGE,"E30")])]}),"instanceName":"19"});
            var Q19;
            Q19=makeQuery(id+"F9.opPattern","COPY",BODY,{"derivedFrom":makeQuery(id+"F7.opExtrude","SWEPT_BODY",BODY,{"disambiguationData":[OSD([sQuery(id+"F6.wireOp",EDGE,"E18"),sQuery(id+"F6.wireOp",EDGE,"E19"),sQuery(id+"F6.wireOp",EDGE,"E20"),sQuery(id+"F6.wireOp",EDGE,"E21"),sQuery(id+"F6.wireOp",EDGE,"E22"),sQuery(id+"F6.wireOp",EDGE,"E23"),sQuery(id+"F6.wireOp",EDGE,"E24"),sQuery(id+"F6.wireOp",EDGE,"E25"),sQuery(id+"F6.wireOp",EDGE,"E26"),sQuery(id+"F6.wireOp",EDGE,"E27"),sQuery(id+"F6.wireOp",EDGE,"E28"),sQuery(id+"F6.wireOp",EDGE,"E29"),sQuery(id+"F6.wireOp",EDGE,"E30")])]}),"instanceName":"20"});
            var Q20;
            Q20=makeQuery(id+"F9.opPattern","COPY",BODY,{"derivedFrom":makeQuery(id+"F7.opExtrude","SWEPT_BODY",BODY,{"disambiguationData":[OSD([sQuery(id+"F6.wireOp",EDGE,"E18"),sQuery(id+"F6.wireOp",EDGE,"E19"),sQuery(id+"F6.wireOp",EDGE,"E20"),sQuery(id+"F6.wireOp",EDGE,"E21"),sQuery(id+"F6.wireOp",EDGE,"E22"),sQuery(id+"F6.wireOp",EDGE,"E23"),sQuery(id+"F6.wireOp",EDGE,"E24"),sQuery(id+"F6.wireOp",EDGE,"E25"),sQuery(id+"F6.wireOp",EDGE,"E26"),sQuery(id+"F6.wireOp",EDGE,"E27"),sQuery(id+"F6.wireOp",EDGE,"E28"),sQuery(id+"F6.wireOp",EDGE,"E29"),sQuery(id+"F6.wireOp",EDGE,"E30")])]}),"instanceName":"22"});
            var Q21;
            Q21=makeQuery(id+"F9.opPattern","COPY",BODY,{"derivedFrom":makeQuery(id+"F7.opExtrude","SWEPT_BODY",BODY,{"disambiguationData":[OSD([sQuery(id+"F6.wireOp",EDGE,"E18"),sQuery(id+"F6.wireOp",EDGE,"E19"),sQuery(id+"F6.wireOp",EDGE,"E20"),sQuery(id+"F6.wireOp",EDGE,"E21"),sQuery(id+"F6.wireOp",EDGE,"E22"),sQuery(id+"F6.wireOp",EDGE,"E23"),sQuery(id+"F6.wireOp",EDGE,"E24"),sQuery(id+"F6.wireOp",EDGE,"E25"),sQuery(id+"F6.wireOp",EDGE,"E26"),sQuery(id+"F6.wireOp",EDGE,"E27"),sQuery(id+"F6.wireOp",EDGE,"E28"),sQuery(id+"F6.wireOp",EDGE,"E29"),sQuery(id+"F6.wireOp",EDGE,"E30")])]}),"instanceName":"2"});
            var Q22;
            Q22=makeQuery(id+"F9.opPattern","COPY",BODY,{"derivedFrom":makeQuery(id+"F7.opExtrude","SWEPT_BODY",BODY,{"disambiguationData":[OSD([sQuery(id+"F6.wireOp",EDGE,"E18"),sQuery(id+"F6.wireOp",EDGE,"E19"),sQuery(id+"F6.wireOp",EDGE,"E20"),sQuery(id+"F6.wireOp",EDGE,"E21"),sQuery(id+"F6.wireOp",EDGE,"E22"),sQuery(id+"F6.wireOp",EDGE,"E23"),sQuery(id+"F6.wireOp",EDGE,"E24"),sQuery(id+"F6.wireOp",EDGE,"E25"),sQuery(id+"F6.wireOp",EDGE,"E26"),sQuery(id+"F6.wireOp",EDGE,"E27"),sQuery(id+"F6.wireOp",EDGE,"E28"),sQuery(id+"F6.wireOp",EDGE,"E29"),sQuery(id+"F6.wireOp",EDGE,"E30")])]}),"instanceName":"1"});
            var Q23;
            Q23=makeQuery(id+"F9.opPattern","COPY",BODY,{"derivedFrom":makeQuery(id+"F7.opExtrude","SWEPT_BODY",BODY,{"disambiguationData":[OSD([sQuery(id+"F6.wireOp",EDGE,"E18"),sQuery(id+"F6.wireOp",EDGE,"E19"),sQuery(id+"F6.wireOp",EDGE,"E20"),sQuery(id+"F6.wireOp",EDGE,"E21"),sQuery(id+"F6.wireOp",EDGE,"E22"),sQuery(id+"F6.wireOp",EDGE,"E23"),sQuery(id+"F6.wireOp",EDGE,"E24"),sQuery(id+"F6.wireOp",EDGE,"E25"),sQuery(id+"F6.wireOp",EDGE,"E26"),sQuery(id+"F6.wireOp",EDGE,"E27"),sQuery(id+"F6.wireOp",EDGE,"E28"),sQuery(id+"F6.wireOp",EDGE,"E29"),sQuery(id+"F6.wireOp",EDGE,"E30")])]}),"instanceName":"23"});
            var Q24;
            Q24=makeQuery(id+"F9.opPattern","COPY",BODY,{"derivedFrom":makeQuery(id+"F7.opExtrude","SWEPT_BODY",BODY,{"disambiguationData":[OSD([sQuery(id+"F6.wireOp",EDGE,"E18"),sQuery(id+"F6.wireOp",EDGE,"E19"),sQuery(id+"F6.wireOp",EDGE,"E20"),sQuery(id+"F6.wireOp",EDGE,"E21"),sQuery(id+"F6.wireOp",EDGE,"E22"),sQuery(id+"F6.wireOp",EDGE,"E23"),sQuery(id+"F6.wireOp",EDGE,"E24"),sQuery(id+"F6.wireOp",EDGE,"E25"),sQuery(id+"F6.wireOp",EDGE,"E26"),sQuery(id+"F6.wireOp",EDGE,"E27"),sQuery(id+"F6.wireOp",EDGE,"E28"),sQuery(id+"F6.wireOp",EDGE,"E29"),sQuery(id+"F6.wireOp",EDGE,"E30")])]}),"instanceName":"18"});
            var Q25;
            Q25=makeQuery(id+"F11.opRevolve","SWEPT_BODY",BODY,{"disambiguationData":[OSD([sQuery(id+"F10.wireOp",EDGE,"E32"),sQuery(id+"F10.wireOp",EDGE,"E34"),sQuery(id+"F10.wireOp",EDGE,"E35"),sQuery(id+"F10.wireOp",EDGE,"E40"),sQuery(id+"F10.wireOp",EDGE,"E41"),sQuery(id+"F10.wireOp",EDGE,"E42"),sQuery(id+"F10.wireOp",EDGE,"E43"),sQuery(id+"F10.wireOp",EDGE,"E44"),sQuery(id+"F10.wireOp",EDGE,"E45"),sQuery(id+"F10.wireOp",EDGE,"E46"),sQuery(id+"F10.wireOp",EDGE,"E47")])]});
            booleanBodies(context, id + "F15", {"operationType" : BooleanOperationType.SUBTRACTION, "tools" : qUnion([Q0, Q1, Q2, Q3, Q4, Q5, Q6, Q7, Q8, Q9, Q10, Q11, Q12, Q13, Q14, Q15, Q16, Q17, Q18, Q19, Q20, Q21, Q22, Q23, Q24]), "targets" : qUnion([Q25]), "offset" : true, "offsetAll" : true, "offsetDistance" : .15 * mm, "keepTools" : true});
        }
    });
